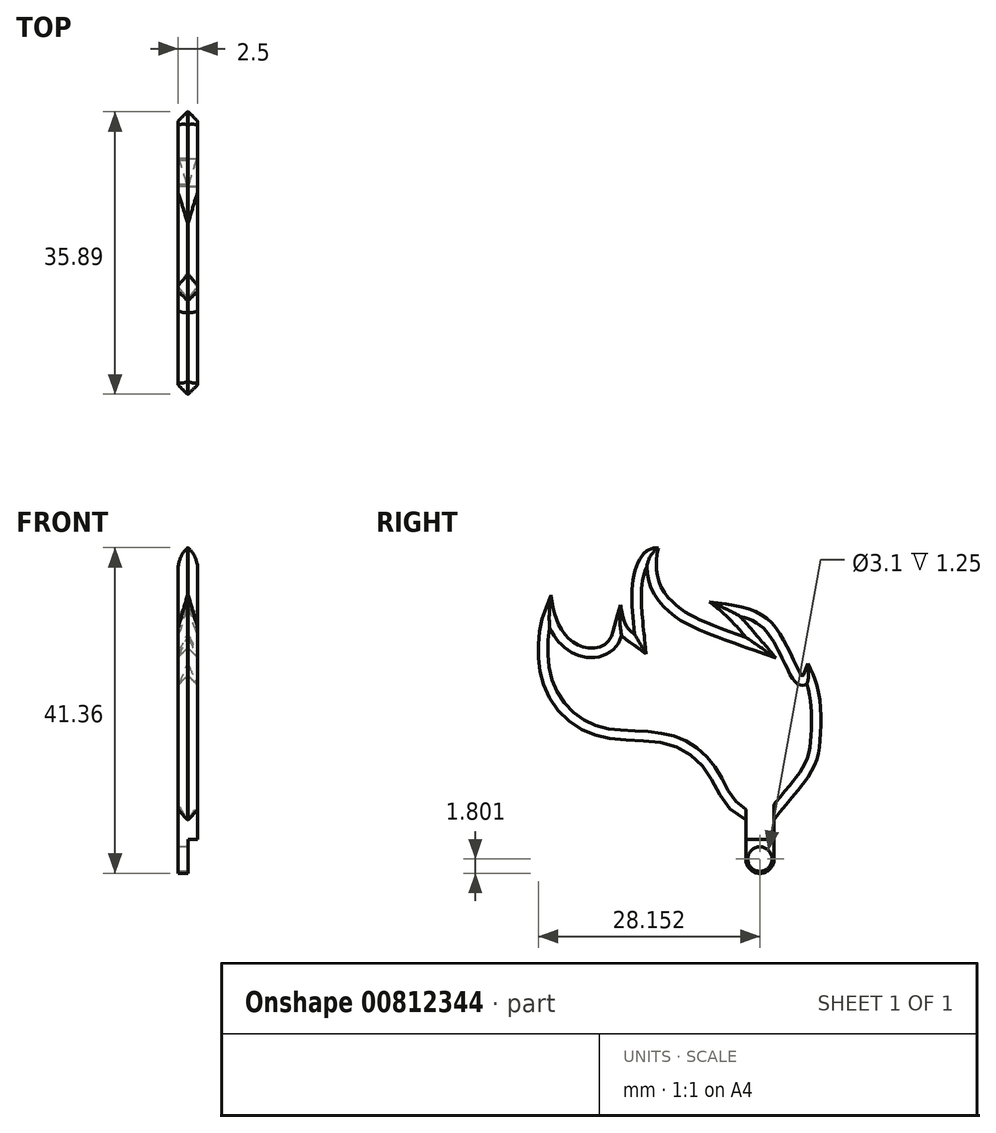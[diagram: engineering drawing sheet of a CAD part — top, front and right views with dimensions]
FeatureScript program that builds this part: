
annotation { "Feature Type Name" : "Feature", "Feature Type Description" : "" }
export const myFeature = defineFeature(function(context is Context, id is Id, definition is map)
    precondition{}
    {
        {
            var Q0;
            Q0=qCreatedBy(makeId("Right.planeOp"),FACE);
            var sketch = newSketch(context, id + "F0", { "sketchPlane" : qUnion([Q0])});
            skFitSpline(sketch, "E0", {"points": [v(-6.32, -4.18) * mm, v(-1.57, 1.96) * mm, v(-0.48, 5.85) * mm, v(-0.7, 12.2) * mm, v(-2.03, 15.65) * mm], "startDerivative": vector(16.9, 22.53) * mm, "endDerivative": vector(-7.48, 14.55) * mm});
            skFitSpline(sketch, "E1", {"points": [v(-2.03, 15.65) * mm, v(-2.66, 14.14) * mm, v(-2.78, 14.14) * mm, v(-4.55, 17.57) * mm, v(-7.87, 21.84) * mm, v(-14.5, 23.5) * mm], "startDerivative": vector(-4.8, -13.6) * mm, "endDerivative": vector(-24.14, 2.94) * mm});
            skFitSpline(sketch, "E2", {"points": [v(-14.5, 23.5) * mm, v(-12.26, 21.6) * mm, v(-9.89, 19) * mm], "startDerivative": vector(4.76, -3.73) * mm, "endDerivative": vector(4.5, -5.26) * mm});
            skFitSpline(sketch, "E3", {"points": [v(-9.89, 19) * mm, v(-16.05, 21.37) * mm, v(-18.54, 22.9) * mm, v(-20.8, 25.63) * mm, v(-21.27, 28.83) * mm, v(-21.03, 30.37) * mm], "startDerivative": vector(-24.8, 8.87) * mm, "endDerivative": vector(2.18, 10.15) * mm});
            skFitSpline(sketch, "E4", {"points": [v(-21.03, 30.37) * mm, v(-22.49, 29.98) * mm, v(-24.16, 26.67) * mm, v(-24.04, 19.42) * mm], "startDerivative": vector(-7.08, -0.44) * mm, "endDerivative": vector(1.77, -16.74) * mm});
            skFitSpline(sketch, "E5", {"points": [v(-24.04, 19.42) * mm, v(-25.06, 20.41) * mm, v(-25.83, 23.13) * mm], "startDerivative": vector(-2.72, 1.92) * mm, "endDerivative": vector(-0.96, 5.31) * mm});
            skFitSpline(sketch, "E6", {"points": [v(-25.83, 23.13) * mm, v(-26.53, 20.63) * mm, v(-27.5, 18.35) * mm, v(-29.96, 17.64) * mm, v(-32.35, 18.78) * mm, v(-33.92, 21.17) * mm, v(-34.63, 24.38) * mm], "startDerivative": vector(-4.5, -15.12) * mm, "endDerivative": vector(-2.72, 18.17) * mm});
            skFitSpline(sketch, "E7", {"points": [v(-34.63, 24.38) * mm, v(-35.92, 20.77) * mm, v(-36.25, 16.54) * mm, v(-35.26, 12.1) * mm, v(-31.72, 7.86) * mm, v(-26.61, 6.07) * mm, v(-19.6, 5.36) * mm, v(-14.64, 1.61) * mm, v(-9.92, -4.18) * mm], "startDerivative": vector(-13.99, -32.97) * mm, "endDerivative": vector(57.4, -23.65) * mm});
            skLineSegment(sketch, "E8.left", {"start": v(-9.92, -4.18) * mm, "end": v(-9.92, -9.18) * mm});
            skLineSegment(sketch, "E8.right", {"start": v(-6.32, -4.18) * mm, "end": v(-6.32, -9.18) * mm});
            skLineSegment(sketch, "E9.trimOffspring", {"start": v(-6.32, -4.18) * mm, "end": v(-6.32, -4.18) * mm});
            skPoint(sketch, "E10.start.orphan", {"position": v(-6.32, -9.18) * mm});
            skPoint(sketch, "E11.start.orphan", {"position": v(-9.92, -9.18) * mm});
            skPoint(sketch, "E12", {"position": v(-8.12, -9.18) * mm});
            skArc(sketch, "E13", {"start": v(-6.32, -9.18) * mm, "mid": v(-8.12, -10.98) * mm, "end": v(-9.92, -9.18) * mm});
            skSolve(sketch);
        }
        {
            var Q0;
            Q0 = qSketchRegion(id + "F0", true);
            extrude(context, id + "F1", {"entities" : qUnion([Q0]), "depth" : 2.5 * mm, "offsetDistance" : 25 * mm, "symmetric" : true});
        }
        {
            var Q0;
            Q0=makeQuery(id+"F1.opExtrude","CAP_EDGE",EDGE,{"disambiguationData":[OSD([sQuery(id+"F0.wireOp",EDGE,"E4")])],"isStart":false});
            var Q1;
            Q1=makeQuery(id+"F1.opExtrude","CAP_EDGE",EDGE,{"disambiguationData":[OSD([sQuery(id+"F0.wireOp",EDGE,"E5")])],"isStart":false});
            var Q2;
            Q2=makeQuery(id+"F1.opExtrude","CAP_EDGE",EDGE,{"disambiguationData":[OSD([sQuery(id+"F0.wireOp",EDGE,"E6")])],"isStart":false});
            var Q3;
            Q3=makeQuery(id+"F1.opExtrude","CAP_EDGE",EDGE,{"disambiguationData":[OSD([sQuery(id+"F0.wireOp",EDGE,"E7")])],"isStart":false});
            var Q4;
            Q4=makeQuery(id+"F1.opExtrude","CAP_EDGE",EDGE,{"disambiguationData":[OSD([sQuery(id+"F0.wireOp",EDGE,"E3")])],"isStart":false});
            var Q5;
            Q5=makeQuery(id+"F1.opExtrude","CAP_EDGE",EDGE,{"disambiguationData":[OSD([sQuery(id+"F0.wireOp",EDGE,"E2")])],"isStart":false});
            var Q6;
            Q6=makeQuery(id+"F1.opExtrude","CAP_EDGE",EDGE,{"disambiguationData":[OSD([sQuery(id+"F0.wireOp",EDGE,"E1")])],"isStart":false});
            var Q7;
            Q7=makeQuery(id+"F1.opExtrude","CAP_EDGE",EDGE,{"disambiguationData":[OSD([sQuery(id+"F0.wireOp",EDGE,"E0")])],"isStart":false});
            var Q8;
            Q8=makeQuery(id+"F1.opExtrude","CAP_EDGE",EDGE,{"disambiguationData":[OSD([sQuery(id+"F0.wireOp",EDGE,"E0")])],"isStart":true});
            var Q9;
            Q9=makeQuery(id+"F1.opExtrude","CAP_EDGE",EDGE,{"disambiguationData":[OSD([sQuery(id+"F0.wireOp",EDGE,"E1")])],"isStart":true});
            var Q10;
            Q10=makeQuery(id+"F1.opExtrude","CAP_EDGE",EDGE,{"disambiguationData":[OSD([sQuery(id+"F0.wireOp",EDGE,"E2")])],"isStart":true});
            var Q11;
            Q11=makeQuery(id+"F1.opExtrude","CAP_EDGE",EDGE,{"disambiguationData":[OSD([sQuery(id+"F0.wireOp",EDGE,"E3")])],"isStart":true});
            var Q12;
            Q12=makeQuery(id+"F1.opExtrude","CAP_EDGE",EDGE,{"disambiguationData":[OSD([sQuery(id+"F0.wireOp",EDGE,"E4")])],"isStart":true});
            var Q13;
            Q13=makeQuery(id+"F1.opExtrude","CAP_EDGE",EDGE,{"disambiguationData":[OSD([sQuery(id+"F0.wireOp",EDGE,"E5")])],"isStart":true});
            var Q14;
            Q14=makeQuery(id+"F1.opExtrude","CAP_EDGE",EDGE,{"disambiguationData":[OSD([sQuery(id+"F0.wireOp",EDGE,"E6")])],"isStart":true});
            var Q15;
            Q15=makeQuery(id+"F1.opExtrude","CAP_EDGE",EDGE,{"disambiguationData":[OSD([sQuery(id+"F0.wireOp",EDGE,"E7")])],"isStart":true});
            chamfer(context, id + "F2", {"entities" : qUnion([Q0, Q1, Q2, Q3, Q4, Q5, Q6, Q7, Q8, Q9, Q10, Q11, Q12, Q13, Q14, Q15]), "width" : 1.2 * mm, "tangentPropagation" : true});
        }
        {
            var Q0;
            Q0=makeQuery(id+"F1.opExtrude","CAP_FACE",FACE,{"disambiguationData":[OSD([sQuery(id+"F0.wireOp",EDGE,"E0"),sQuery(id+"F0.wireOp",EDGE,"E1"),sQuery(id+"F0.wireOp",EDGE,"E2"),sQuery(id+"F0.wireOp",EDGE,"E3"),sQuery(id+"F0.wireOp",EDGE,"E4"),sQuery(id+"F0.wireOp",EDGE,"E5"),sQuery(id+"F0.wireOp",EDGE,"E6"),sQuery(id+"F0.wireOp",EDGE,"E7"),sQuery(id+"F0.wireOp",EDGE,"E8.left"),sQuery(id+"F0.wireOp",EDGE,"E8.right"),sQuery(id+"F0.wireOp",EDGE,"E13")])],"isStart":true});
            var sketch = newSketch(context, id + "F3", { "sketchPlane" : qUnion([Q0])});
            skCircle(sketch, "E14", {"center": v(8.12, -9.18) * mm, "radius": 1.55 * mm});
            skSolve(sketch);
        }
        {
            var Q0;
            Q0 = qSketchRegion(id + "F3", true);
            extrude(context, id + "F4", {"entities" : qUnion([Q0]), "operationType" : NewBodyOperationType.REMOVE, "endBound" : BoundingType.UP_TO_NEXT, "oppositeDirection" : true, "depth" : 5 * mm, "offsetDistance" : 25 * mm});
        }
        {
            var Q0;
            Q0=makeQuery(id+"F1.opExtrude","CAP_FACE",FACE,{"disambiguationData":[OSD([sQuery(id+"F0.wireOp",EDGE,"E0"),sQuery(id+"F0.wireOp",EDGE,"E1"),sQuery(id+"F0.wireOp",EDGE,"E2"),sQuery(id+"F0.wireOp",EDGE,"E3"),sQuery(id+"F0.wireOp",EDGE,"E4"),sQuery(id+"F0.wireOp",EDGE,"E5"),sQuery(id+"F0.wireOp",EDGE,"E6"),sQuery(id+"F0.wireOp",EDGE,"E7"),sQuery(id+"F0.wireOp",EDGE,"E8.left"),sQuery(id+"F0.wireOp",EDGE,"E8.right"),sQuery(id+"F0.wireOp",EDGE,"E13")])],"isStart":false});
            var sketch = newSketch(context, id + "F5", { "sketchPlane" : qUnion([Q0])});
            skLineSegment(sketch, "E15", {"start": v(-9.92, -6.68) * mm, "end": v(-6.32, -6.68) * mm});
            skLineSegment(sketch, "E16", {"start": v(-6.32, -6.68) * mm, "end": v(-6.32, -9.18) * mm});
            skLineSegment(sketch, "E17", {"start": v(-9.92, -6.68) * mm, "end": v(-9.92, -9.18) * mm});
            skArc(sketch, "E18", {"start": v(-9.92, -9.18) * mm, "mid": v(-8.12, -10.98) * mm, "end": v(-6.32, -9.18) * mm});
            skSolve(sketch);
        }
        {
            var Q0;
            Q0 = qSketchRegion(id + "F5", true);
            extrude(context, id + "F6", {"entities" : qUnion([Q0]), "operationType" : NewBodyOperationType.REMOVE, "oppositeDirection" : true, "depth" : 1.25 * mm, "offsetDistance" : 25 * mm});
        }
    });
